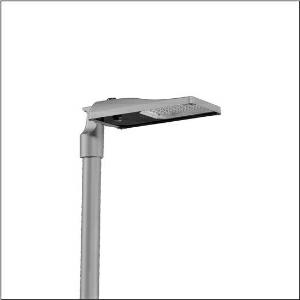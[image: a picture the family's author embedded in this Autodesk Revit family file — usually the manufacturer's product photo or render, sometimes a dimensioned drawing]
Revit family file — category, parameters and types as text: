
# Revit family: streetlight_sl_31_mini___stw1_0a_5xh6e31t08ha_3957
name_source: partatom
category: Lighting Fixtures
units: mm (PartAtom-declared; Revit-internal decimal feet)

## family parameters
Cut with Voids When Loaded = No
Host = Face
Light Source = No
Part Type = Normal
Room Calculation Point = No
Round Connector Dimension = Use Diameter
Shared = No

## types (1)
- --- (1 x LED, 9230 lm, 68.3 W, 3000K)
    Apparent Load = 68 VA
    CIE Flux Codes = 38 75 98 100 100
    Color Rendering = 70
    Color Temperature = 3000K
    Default Elevation = 1800 mm
    Description = Streetlight SL 31 mini D4i, Desk-Remote mast luminaire for post-top, side-entry; light control with lens of PMMA; light distribution: STW1.0a, direct asymmetric distribution, for standard-compliant lighting for roads and squares; LED: luminous flux: 9.230lm, light colour: 730, colour temperature: 3000K; luminous efficacy: 135,1lm/W; control: pre-setting: logarithmic dimming characteristic, flexible luminous flux parameterisation, time-dependent luminous flux control, constant luminous flux control, power reduction, intelligent temperature release in ECG and LED module, overheat protection; luminaire housing, of diecast aluminium, SITECO metallic grey (DB 702S), corrosivity category C5 high according to DIN EN ISO 12944; cover of toughened safety glass, transparent, opened without tools; mast flange of diecast aluminium, SITECO metallic grey (DB 702S), spigot size: 76/60mm, mast flange included unmounted; cable length: 8,5m, connection cable pre-assembled; mains connection: 220..240V, AC, 50/60Hz; power consumption (at start of service life): 68,3W / (at end of service life): 74,5W / (with reduced operation 50%): 29,5W; protection rating (complete): IP66; insulation class (complete): insulation class II (safety insulation); impact resistance: IK09; certification: CE, ENEC, ENEC+, VDE, UKCA, ZD4i; permissible operating ambient temperature for outdoor applications: -40..+50°C; packaging unit: 1 piece

Light Distribution: STW1.0a
    Height = 76 mm
    Lamp = 1 x LED
    Lamp Light Flux = 9230 lm
    Lamp Power = 68.3 W
    Lamp count = 1
    Length = 547 mm
    Luminous efficacy = 135 lm/W
    Manufacturer = Siteco
    ModVariant = No
    Model = 5XH6E31T08HA
    Number of Poles = 1
    OnlyDefault = Yes
    Power Factor = 1
    Product Name = Streetlight SL 31 mini | STW1.0a
    Product group = mast luminaire | pylon top
    ProductGroupID = 6100
    Protection Class = Protection class II
    Protection Degree = IP 66
    RLX_Detail_Level = 1
    RLX_Emergency_Light_Flux = 0 lm
    RLX_Emergency_Type = 0
    RLX_Emergency_Type_DB = No
    RlxData = <blob elided: 24289 chars, md5=e33742ef>
    Socket = socket
    Standby Power = 0 W
    System Light Flux = 9230 lm
    System Power = 68 W
    Type Comments = factory setting: luminous flux: 100 % | dim-lin: 254 | 692 mA
    Type Image = l_1300332.jpg
    URL = http://relux.com
    VarID = @adj_020131
    Voltage = 0 V
    Weight = 0.00 kg
    Width = 265 mm

## geometry (parser evidence)
native form markers: Blend x4, Sweep x9
no freeform markers — native parametric forms only
